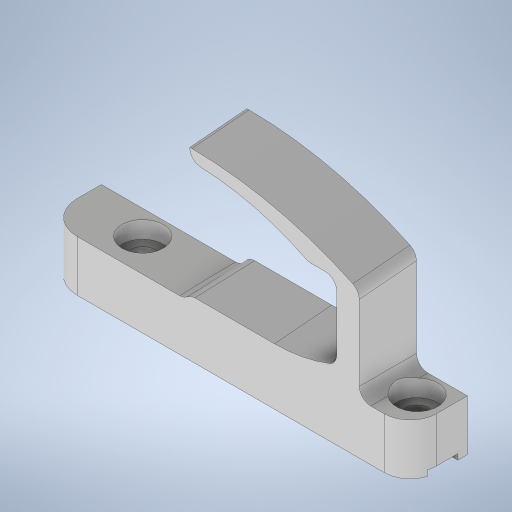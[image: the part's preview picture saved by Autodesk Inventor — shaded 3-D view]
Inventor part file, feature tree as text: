
AUTODESK INVENTOR PART (.ipt)
format: ipt  version: 2024 (Build 280153000, 153)  size: 661,504 bytes
history: native  units: mm
features: extrude x9, sketch x7, projected_geometry x2, plane x1, fillet x1
ambient origin geometry x8: Origin, YZ Plane, XZ Plane, XY Plane, X Axis, Y Axis, Z Axis, Center Point
bodies: Solid1 (feature_tree)
feature tree (20):
  sketch  "Sketch6"  dims[d31=30.0mm d32=0.0mm d33=11.0mm]
  plane  "Work Plane2"
  extrude  "Extrusion7"  Depth=0.872665mm
  extrude  "Extrusion8"  Depth=11.0mm
  extrude  "Extrusion9"  Depth=5.0mm
  sketch  "Sketch10"  dims[d44=2.0mm d45=1.5mm d46=0.0mm]
  extrude  "Extrusion10"  Depth=5.0mm
  extrude  "Extrusion11"  Depth=10.9mm TaperAngle=0.0deg
  fillet  "Fillet1"  Radius=10.0mm
  extrude  "Extrusion12"  Depth=1.5mm TaperAngle=0.0deg
  sketch  "Sketch7"  dims[d34=15.5mm d35=0.0mm d36=5.0mm]
  sketch  "Sketch8"  dims[d37=2.0mm d38=5.0mm]
  sketch  "Sketch9"  dims[d39=2.4mm d40=10.9mm d41=0.0mm d42=10.0mm d43=0.0mm]
  projected_geometry  "Projected Loop3"
  projected_geometry  "Projected Loop4"
  sketch  "Sketch11"  dims[d47=1.0mm d48=0.0mm]
  sketch  "Sketch1"  dims[d0=10.0mm d1=3.2mm d2=1.0mm d3=3.0mm d4=7.3mm d5=3.2mm d6=4.1mm d7=48.5mm d9=0.0mm d10=1.0mm d12=0.0mm d13=8.0mm d15=0.0mm d16=5.0mm d30=0.872665mm]
  extrude  "Extrusion1"  [1 undecoded]
  extrude  "Extrusion2"  [1 undecoded]
  extrude  "Extrusion3"  [1 undecoded]
note: 3 required parameter values undecoded (feature->parameter linkage not recoverable at this tier; creation-order binding heuristic only, values carry confidence <= 0.55)
